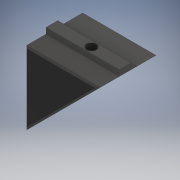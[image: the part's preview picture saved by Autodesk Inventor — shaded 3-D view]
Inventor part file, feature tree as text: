
AUTODESK INVENTOR PART (.ipt)
format: ipt  version: 2017.3 (Build 213256000, 256)  size: 169,984 bytes
history: native  units: mm
features: extrude x6, sketch x6, chamfer x4
ambient origin geometry x8: Origin, YZ Plane, XZ Plane, XY Plane, X Axis, Y Axis, Z Axis, Center Point
bodies: Solid1 (feature_tree)
feature tree (16):
  extrude  "Extrusion1"  Depth=20.0mm TaperAngle=0.0deg
  extrude  "Extrusion2"  Depth=3.0mm
  extrude  "Extrusion5"  Depth=4.0mm
  extrude  "Extrusion6"  Depth=1.0mm TaperAngle=0.0deg
  chamfer  "Chamfer4"  Distance=1.0mm Angle=45.0deg
  extrude  "Extrusion7"  Depth=1.0mm TaperAngle=0.0deg
  extrude  "Extrusion8"  Depth=1.0mm TaperAngle=0.0deg
  chamfer  "Chamfer5"  Distance=1.0mm Angle=45.0deg
  chamfer  "Chamfer6"  Distance=2.0mm Angle=45.0deg
  chamfer  "Chamfer7"  Distance=0.5mm Angle=45.0deg
  sketch  "Sketch1"  dims[d0=25.0mm d1=20.0mm d2=0.0mm]
  sketch  "Sketch2"  dims[d3=3.0mm d4=3.0mm]
  sketch  "Sketch5"  dims[d5=17.0mm d6=0.0mm d22=4.0mm]
  sketch  "Sketch6"  dims[d23=1.0mm d24=0.0mm d25=1.0mm d26=0.0mm d27=1.0mm d28=2.0mm d29=45.0deg]
  sketch  "Sketch7"  dims[d30=3.4mm d31=1.0mm d32=0.0mm]
  sketch  "Sketch8"  dims[d33=3.4mm d34=1.0mm d35=0.0mm d36=1.0mm d37=2.0mm d38=45.0deg d39=2.0mm d40=2.0mm d41=45.0deg d42=0.5mm d43=2.0mm d44=45.0deg]
